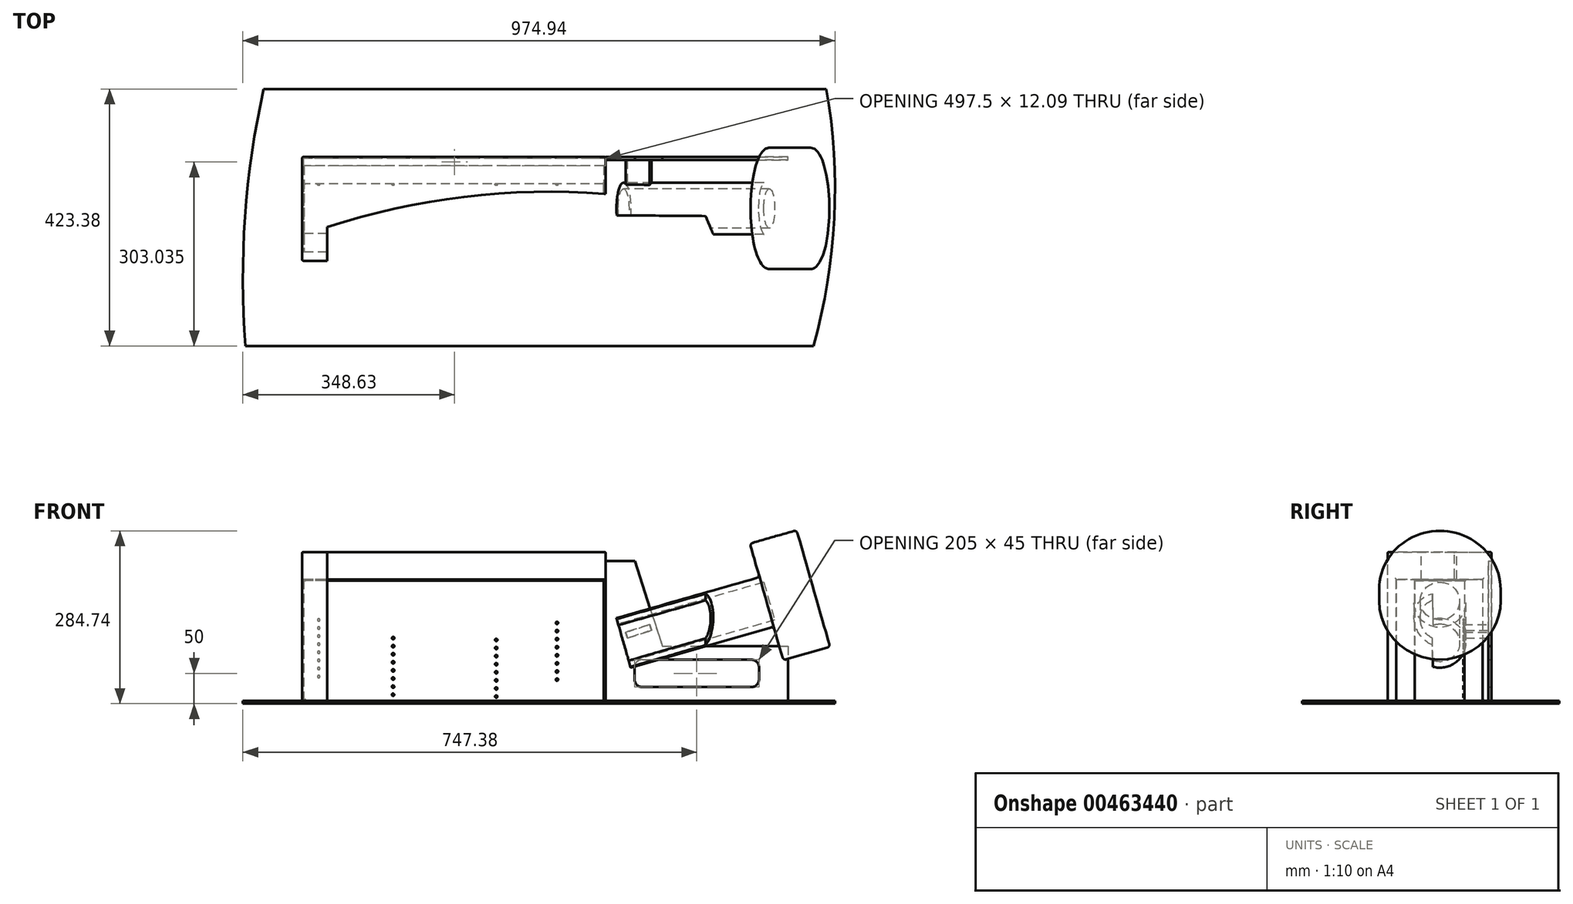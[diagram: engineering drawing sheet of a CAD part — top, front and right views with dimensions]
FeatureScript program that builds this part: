
annotation { "Feature Type Name" : "Feature", "Feature Type Description" : "" }
export const myFeature = defineFeature(function(context is Context, id is Id, definition is map)
    precondition{}
    {
        {
            var Q0;
            Q0=qCreatedBy(makeId("Right.planeOp"),FACE);
            var sketch = newSketch(context, id + "F0", { "sketchPlane" : qUnion([Q0])});
            skLineSegment(sketch, "E0.top", {"start": v(-171.18, 245.1) * mm, "end": v(0, 245.1) * mm});
            skLineSegment(sketch, "E0.left", {"start": v(-171.18, 0) * mm, "end": v(-171.18, 245.1) * mm});
            skLineSegment(sketch, "E0.right", {"start": v(0, 0) * mm, "end": v(0, 245.1) * mm});
            skLineSegment(sketch, "E1", {"start": v(-171.18, 0) * mm, "end": v(-156.6, 0) * mm});
            skLineSegment(sketch, "E2", {"start": v(-156.6, 0) * mm, "end": v(-156.6, 200) * mm});
            skLineSegment(sketch, "E3", {"start": v(-156.6, 200) * mm, "end": v(-14.59, 200) * mm});
            skLineSegment(sketch, "E4", {"start": v(-14.59, 200) * mm, "end": v(-14.59, 0) * mm});
            skLineSegment(sketch, "E5", {"start": v(-14.59, 0) * mm, "end": v(0, 0) * mm});
            skSolve(sketch);
        }
        {
            var Q0;
            Q0=makeQuery(id+"F0.imprint","IMPRINT",FACE,{"disambiguationData":[TD([[makeQuery(id+"F0.imprint","IMPRINT",EDGE,{"derivedFrom":sQuery(id+"F0.wireOp",EDGE,"E0.top")}),-1.0]])]});
            extrude(context, id + "F1", {"entities" : qUnion([Q0]), "depth" : 496.5 * mm, "hasSecondDirection" : true, "secondDirectionOppositeDirection" : true, "secondDirectionDepth" : 3.5 * mm});
        }
        {
            var Q0;
            Q0=qCreatedBy(makeId("Right.planeOp"),FACE);
            var sketch = newSketch(context, id + "F2", { "sketchPlane" : qUnion([Q0])});
            skLineSegment(sketch, "E6.bottom", {"start": v(-14.59, 0) * mm, "end": v(-44.59, 0) * mm});
            skLineSegment(sketch, "E6.top", {"start": v(-14.6, 200) * mm, "end": v(-156.6, 200) * mm});
            skLineSegment(sketch, "E6.left", {"start": v(-14.59, 0) * mm, "end": v(-14.6, 200) * mm});
            skLineSegment(sketch, "E6.right", {"start": v(-156.59, 0) * mm, "end": v(-156.6, 200) * mm});
            skLineSegment(sketch, "E7", {"start": v(-126.59, 0) * mm, "end": v(-126.59, 198) * mm});
            skLineSegment(sketch, "E8", {"start": v(-126.59, 198) * mm, "end": v(-44.6, 198) * mm});
            skLineSegment(sketch, "E9", {"start": v(-44.6, 198) * mm, "end": v(-44.59, 0) * mm});
            skLineSegment(sketch, "E10.trimOffspring", {"start": v(-126.59, 0) * mm, "end": v(-156.59, 0) * mm});
            skSolve(sketch);
        }
        {
            var Q0;
            Q0 = qSketchRegion(id + "F2", true);
            extrude(context, id + "F3", {"entities" : qUnion([Q0]), "depth" : 493 * mm});
        }
        {
            var Q0;
            Q0=makeQuery(id+"F1.opExtrude","SWEPT_FACE",FACE,{"disambiguationData":[OSD([sQuery(id+"F0.wireOp",EDGE,"E0.top")])]});
            var sketch = newSketch(context, id + "F4", { "sketchPlane" : qUnion([Q0])});
            skLineSegment(sketch, "E11", {"start": v(37.8, -115.66) * mm, "end": v(37.8, -234.3) * mm});
            skLineSegment(sketch, "E12", {"start": v(37.8, -234.3) * mm, "end": v(505.15, -234.3) * mm});
            skLineSegment(sketch, "E13", {"start": v(509.32, -61.9) * mm, "end": v(505.15, -234.3) * mm});
            skArc(sketch, "E14", {"start": v(509.32, -61.9) * mm, "mid": v(270.84, -64.96) * mm, "end": v(37.8, -115.66) * mm});
            skSolve(sketch);
        }
        {
            var Q0;
            {var subQ0=sQuery(id+"F4.wireOp",EDGE,"E14");var subQ1=sQuery(id+"F4.wireOp",EDGE,"E11");var subQ2=makeQuery(id+"F4.imprint","INTERSECT",VERTEX,{"derivedFrom":[subQ1,subQ0]});Q0=makeQuery(id+"F4.imprint","IMPRINT",FACE,{"disambiguationData":[TD([[makeQuery(id+"F4.imprint","IMPRINT",EDGE,{"disambiguationData":[TD([[subQ2,1.0]])],"derivedFrom":subQ0}),1.0]])]});}
            extrude(context, id + "F5", {"entities" : qUnion([Q0]), "operationType" : NewBodyOperationType.REMOVE, "endBound" : BoundingType.THROUGH_ALL, "oppositeDirection" : true, "depth" : 25 * mm, "hasSecondDirection" : true, "secondDirectionBound" : SecondDirectionBoundingType.THROUGH_ALL, "secondDirectionOppositeDirection" : false, "secondDirectionDepth" : 25 * mm});
        }
        {
            var Q0;
            Q0=makeQuery(id+"F3.opExtrude","SWEPT_FACE",FACE,{"disambiguationData":[OSD([sQuery(id+"F2.wireOp",EDGE,"E9")])]});
            var sketch = newSketch(context, id + "F6", { "sketchPlane" : qUnion([Q0])});
            skCircle(sketch, "E15", {"center": v(24, 39.75) * mm, "radius": 2 * mm});
            skCircle(sketch, "E16.1.0.0", {"center": v(24, 53.1) * mm, "radius": 2 * mm});
            skCircle(sketch, "E16.2.0.0", {"center": v(24, 66.43) * mm, "radius": 2 * mm});
            skCircle(sketch, "E16.3.0.0", {"center": v(24, 79.77) * mm, "radius": 2 * mm});
            skCircle(sketch, "E16.4.0.0", {"center": v(24, 93.11) * mm, "radius": 2 * mm});
            skCircle(sketch, "E16.5.0.0", {"center": v(24, 106.45) * mm, "radius": 2 * mm});
            skCircle(sketch, "E16.6.0.0", {"center": v(24, 119.79) * mm, "radius": 2 * mm});
            skCircle(sketch, "E16.7.0.0", {"center": v(24, 133.13) * mm, "radius": 2 * mm});
            skLineSegment(sketch, "E16.direction1", {"start": v(24, 39.75) * mm, "end": v(24, 53.1) * mm, "construction": true});
            skCircle(sketch, "E17", {"center": v(146.3, 9.75) * mm, "radius": 2 * mm});
            skCircle(sketch, "E18.1.0.0", {"center": v(146.35, 23.09) * mm, "radius": 2 * mm});
            skCircle(sketch, "E18.2.0.0", {"center": v(146.4, 36.43) * mm, "radius": 2 * mm});
            skCircle(sketch, "E18.3.0.0", {"center": v(146.46, 49.77) * mm, "radius": 2 * mm});
            skCircle(sketch, "E18.4.0.0", {"center": v(146.51, 63.1) * mm, "radius": 2 * mm});
            skCircle(sketch, "E18.5.0.0", {"center": v(146.57, 76.45) * mm, "radius": 2 * mm});
            skCircle(sketch, "E18.6.0.0", {"center": v(146.62, 89.79) * mm, "radius": 2 * mm});
            skCircle(sketch, "E18.7.0.0", {"center": v(146.67, 103.13) * mm, "radius": 2 * mm});
            skLineSegment(sketch, "E18.direction1", {"start": v(146.3, 9.75) * mm, "end": v(146.35, 23.09) * mm, "construction": true});
            skCircle(sketch, "E19", {"center": v(316.3, 6.75) * mm, "radius": 2 * mm});
            skCircle(sketch, "E20.0.1.0", {"center": v(316.3, 20.09) * mm, "radius": 2 * mm});
            skCircle(sketch, "E20.0.2.0", {"center": v(316.3, 33.43) * mm, "radius": 2 * mm});
            skCircle(sketch, "E20.0.3.0", {"center": v(316.3, 46.77) * mm, "radius": 2 * mm});
            skCircle(sketch, "E20.0.4.0", {"center": v(316.3, 60.1) * mm, "radius": 2 * mm});
            skCircle(sketch, "E20.0.5.0", {"center": v(316.3, 73.45) * mm, "radius": 2 * mm});
            skCircle(sketch, "E20.0.6.0", {"center": v(316.3, 86.79) * mm, "radius": 2 * mm});
            skCircle(sketch, "E20.0.7.0", {"center": v(316.3, 100.13) * mm, "radius": 2 * mm});
            skLineSegment(sketch, "E20.direction1", {"start": v(316.3, 6.75) * mm, "end": v(368.2, 6.75) * mm, "construction": true});
            skLineSegment(sketch, "E20.direction2", {"start": v(316.3, 6.75) * mm, "end": v(316.3, 20.09) * mm, "construction": true});
            skCircle(sketch, "E21", {"center": v(416.3, 34.75) * mm, "radius": 2 * mm});
            skCircle(sketch, "E22.0.1.0", {"center": v(416.3, 48.1) * mm, "radius": 2 * mm});
            skCircle(sketch, "E22.0.2.0", {"center": v(416.3, 61.43) * mm, "radius": 2 * mm});
            skCircle(sketch, "E22.0.3.0", {"center": v(416.3, 74.77) * mm, "radius": 2 * mm});
            skCircle(sketch, "E22.0.4.0", {"center": v(416.3, 88.11) * mm, "radius": 2 * mm});
            skCircle(sketch, "E22.0.5.0", {"center": v(416.3, 101.45) * mm, "radius": 2 * mm});
            skCircle(sketch, "E22.0.6.0", {"center": v(416.3, 114.79) * mm, "radius": 2 * mm});
            skCircle(sketch, "E22.0.7.0", {"center": v(416.3, 128.13) * mm, "radius": 2 * mm});
            skLineSegment(sketch, "E22.direction1", {"start": v(416.3, 34.75) * mm, "end": v(490.5, 34.75) * mm, "construction": true});
            skLineSegment(sketch, "E22.direction2", {"start": v(416.3, 34.75) * mm, "end": v(416.3, 48.1) * mm, "construction": true});
            skSolve(sketch);
        }
        {
            var Q0;
            Q0 = qSketchRegion(id + "F6", true);
            extrude(context, id + "F7", {"entities" : qUnion([Q0]), "depth" : 2 * mm});
        }
        {
            var Q0;
            Q0=makeQuery(id+"F1.opExtrude","SWEPT_EDGE",EDGE,{"disambiguationData":[OSD([sQuery(id+"F0.wireOp",EDGE,"E0.top"),sQuery(id+"F0.wireOp",EDGE,"E0.left")])]});
            var Q1;
            Q1=makeQuery(id+"F1.opExtrude","CAP_EDGE",EDGE,{"disambiguationData":[OSD([sQuery(id+"F0.wireOp",EDGE,"E0.top")])],"isStart":true});
            var Q2;
            Q2=makeQuery(id+"F1.opExtrude","SWEPT_EDGE",EDGE,{"disambiguationData":[OSD([sQuery(id+"F0.wireOp",EDGE,"E0.top"),sQuery(id+"F0.wireOp",EDGE,"E0.right")])]});
            var Q3;
            Q3=makeQuery(id+"F1.opExtrude","CAP_EDGE",EDGE,{"disambiguationData":[OSD([sQuery(id+"F0.wireOp",EDGE,"E0.left")])],"isStart":true});
            var Q4;
            Q4=makeQuery(id+"F1.opExtrude","CAP_EDGE",EDGE,{"disambiguationData":[OSD([sQuery(id+"F0.wireOp",EDGE,"E0.right")])],"isStart":false});
            var Q5;
            Q5=makeQuery(id+"F1.opExtrude","CAP_EDGE",EDGE,{"disambiguationData":[OSD([sQuery(id+"F0.wireOp",EDGE,"E0.top")])],"isStart":false});
            var Q6;
            Q6=makeQuery(id+"F1.opExtrude","CAP_EDGE",EDGE,{"disambiguationData":[OSD([sQuery(id+"F0.wireOp",EDGE,"E4")])],"isStart":false});
            var Q7;
            Q7=makeQuery(id+"F1.opExtrude","CAP_EDGE",EDGE,{"disambiguationData":[OSD([sQuery(id+"F0.wireOp",EDGE,"E3")])],"isStart":false});
            var Q8;
            Q8=makeQuery(id+"F1.opExtrude","SWEPT_EDGE",EDGE,{"disambiguationData":[OSD([sQuery(id+"F0.wireOp",EDGE,"E0.right"),sQuery(id+"F0.wireOp",EDGE,"E5")])]});
            var Q9;
            Q9=makeQuery(id+"F1.opExtrude","CAP_EDGE",EDGE,{"disambiguationData":[OSD([sQuery(id+"F0.wireOp",EDGE,"E0.right")])],"isStart":true});
            var Q10;
            Q10=makeQuery(id+"F1.opExtrude","CAP_EDGE",EDGE,{"disambiguationData":[OSD([sQuery(id+"F0.wireOp",EDGE,"E4")])],"isStart":true});
            var Q11;
            Q11=makeQuery(id+"F1.opExtrude","CAP_EDGE",EDGE,{"disambiguationData":[OSD([sQuery(id+"F0.wireOp",EDGE,"E3")])],"isStart":true});
            var Q12;
            Q12=makeQuery(id+"F1.opExtrude","CAP_EDGE",EDGE,{"disambiguationData":[OSD([sQuery(id+"F0.wireOp",EDGE,"E2")])],"isStart":true});
            var Q13;
            Q13=makeQuery(id+"F1.opExtrude","CAP_EDGE",EDGE,{"disambiguationData":[OSD([sQuery(id+"F0.wireOp",EDGE,"E1")])],"isStart":true});
            var Q14;
            Q14=makeQuery(id+"F1.opExtrude","SWEPT_EDGE",EDGE,{"disambiguationData":[OSD([sQuery(id+"F0.wireOp",EDGE,"E0.left"),sQuery(id+"F0.wireOp",EDGE,"E1")])]});
            var Q15;
            Q15=makeQuery(id+"F1.opExtrude","CAP_EDGE",EDGE,{"disambiguationData":[OSD([sQuery(id+"F0.wireOp",EDGE,"E5")])],"isStart":true});
            var Q16;
            Q16=makeQuery(id+"F3.opExtrude","CAP_EDGE",EDGE,{"disambiguationData":[OSD([sQuery(id+"F2.wireOp",EDGE,"E9")])],"isStart":true});
            var Q17;
            Q17=makeQuery(id+"F3.opExtrude","SWEPT_EDGE",EDGE,{"disambiguationData":[OSD([sQuery(id+"F2.wireOp",EDGE,"E6.bottom"),sQuery(id+"F2.wireOp",EDGE,"E9")])]});
            fillet(context, id + "F8", {"entities" : qUnion([Q0, Q1, Q2, Q3, Q4, Q5, Q6, Q7, Q8, Q9, Q10, Q11, Q12, Q13, Q14, Q15, Q16, Q17]), "radius" : 2.5 * mm, "tangentPropagation" : true, "allowEdgeOverflow" : false});
        }
        {
            var Q0;
            Q0=qCreatedBy(makeId("Front.planeOp"),FACE);
            var sketch = newSketch(context, id + "F9", { "sketchPlane" : qUnion([Q0])});
            skLineSegment(sketch, "E23", {"start": v(496.5, 0) * mm, "end": v(496.5, 230) * mm});
            skLineSegment(sketch, "E24", {"start": v(496.5, 230) * mm, "end": v(544.38, 230) * mm});
            skLineSegment(sketch, "E25", {"start": v(544.38, 230) * mm, "end": v(589.8, 90) * mm});
            skLineSegment(sketch, "E26", {"start": v(589.8, 90) * mm, "end": v(796.5, 90) * mm});
            skLineSegment(sketch, "E27", {"start": v(796.5, 90) * mm, "end": v(796.5, 0) * mm});
            skLineSegment(sketch, "E28", {"start": v(796.5, 0) * mm, "end": v(496.5, 0) * mm});
            skLineSegment(sketch, "E29.bottom", {"start": v(556.5, 67.5) * mm, "end": v(736.5, 67.5) * mm});
            skLineSegment(sketch, "E29.top", {"start": v(556.5, 22.5) * mm, "end": v(736.5, 22.5) * mm});
            skLineSegment(sketch, "E29.left", {"start": v(544, 55) * mm, "end": v(544, 35) * mm});
            skLineSegment(sketch, "E29.right", {"start": v(749, 55) * mm, "end": v(749, 35) * mm});
            skPoint(sketch, "E30.visualSharp", {"position": v(544, 67.5) * mm});
            skArc(sketch, "E30.filletArc", {"start": v(556.5, 67.5) * mm, "mid": v(547.66, 63.84) * mm, "end": v(544, 55) * mm});
            skPoint(sketch, "E31.visualSharp", {"position": v(749, 67.5) * mm});
            skArc(sketch, "E31.filletArc", {"start": v(749, 55) * mm, "mid": v(745.34, 63.84) * mm, "end": v(736.5, 67.5) * mm});
            skPoint(sketch, "E32.visualSharp", {"position": v(749, 22.5) * mm});
            skArc(sketch, "E32.filletArc", {"start": v(736.5, 22.5) * mm, "mid": v(745.34, 26.16) * mm, "end": v(749, 35) * mm});
            skPoint(sketch, "E33.visualSharp", {"position": v(544, 22.5) * mm});
            skArc(sketch, "E33.filletArc", {"start": v(544, 35) * mm, "mid": v(547.66, 26.16) * mm, "end": v(556.5, 22.5) * mm});
            skSolve(sketch);
        }
        {
            var Q0;
            Q0 = qSketchRegion(id + "F9", true);
            extrude(context, id + "F10", {"entities" : qUnion([Q0]), "depth" : 5 * mm});
        }
        {
            var Q0;
            Q0=makeQuery(id+"F10.opExtrude","CAP_FACE",FACE,{"disambiguationData":[OSD([sQuery(id+"F9.wireOp",EDGE,"E23"),sQuery(id+"F9.wireOp",EDGE,"E24"),sQuery(id+"F9.wireOp",EDGE,"E25"),sQuery(id+"F9.wireOp",EDGE,"E26"),sQuery(id+"F9.wireOp",EDGE,"E27"),sQuery(id+"F9.wireOp",EDGE,"E28"),sQuery(id+"F9.wireOp",EDGE,"E29.bottom"),sQuery(id+"F9.wireOp",EDGE,"E29.top"),sQuery(id+"F9.wireOp",EDGE,"E29.left"),sQuery(id+"F9.wireOp",EDGE,"E29.right"),sQuery(id+"F9.wireOp",EDGE,"E30.filletArc"),sQuery(id+"F9.wireOp",EDGE,"E31.filletArc"),sQuery(id+"F9.wireOp",EDGE,"E32.filletArc"),sQuery(id+"F9.wireOp",EDGE,"E33.filletArc")])],"isStart":false});
            cPlane(context, id + "F11", {"entities" : qUnion([Q0]), "cplaneType" : CPlaneType.OFFSET, "offset" : 80 * mm, "width" : 150 * mm, "height" : 150 * mm});
        }
        {
            var Q0;
            Q0=qCreatedBy(id+"F11.planeOp",FACE);
            var sketch = newSketch(context, id + "F12", { "sketchPlane" : qUnion([Q0])});
            skLineSegment(sketch, "E34", {"start": v(121.27, 85.77) * mm, "end": v(1213.1, 85.77) * mm, "construction": true});
            skLineSegment(sketch, "E35", {"start": v(226.38, 9.32) * mm, "end": v(1190.67, 285.82) * mm, "construction": true});
            skLineSegment(sketch, "E36", {"start": v(838.36, 184.8) * mm, "end": v(812.17, 276.12) * mm});
            skLineSegment(sketch, "E37", {"start": v(805.99, 279.55) * mm, "end": v(738.7, 260.25) * mm});
            skLineSegment(sketch, "E38", {"start": v(735.27, 254.07) * mm, "end": v(748.36, 208.4) * mm});
            skLineSegment(sketch, "E39", {"start": v(744.93, 202.22) * mm, "end": v(514.23, 136.07) * mm});
            skLineSegment(sketch, "E40", {"start": v(514.23, 136.07) * mm, "end": v(516.99, 126.46) * mm});
            skLineSegment(sketch, "E41", {"start": v(516.99, 126.46) * mm, "end": v(756.84, 195.23) * mm});
            skLineSegment(sketch, "E42", {"start": v(756.84, 195.23) * mm, "end": v(765.8, 164) * mm});
            skPoint(sketch, "E43.visualSharp", {"position": v(733.9, 258.87) * mm});
            skArc(sketch, "E43.filletArc", {"start": v(738.7, 260.25) * mm, "mid": v(735.7, 257.87) * mm, "end": v(735.27, 254.07) * mm});
            skPoint(sketch, "E44.visualSharp", {"position": v(810.8, 280.93) * mm});
            skArc(sketch, "E44.filletArc", {"start": v(812.17, 276.12) * mm, "mid": v(809.79, 279.11) * mm, "end": v(805.99, 279.55) * mm});
            skLineSegment(sketch, "E45", {"start": v(765.8, 164) * mm, "end": v(838.36, 184.8) * mm});
            skPoint(sketch, "E46.visualSharp", {"position": v(749.74, 203.6) * mm});
            skArc(sketch, "E46.filletArc", {"start": v(744.93, 202.22) * mm, "mid": v(747.93, 204.6) * mm, "end": v(748.36, 208.4) * mm});
            skSolve(sketch);
        }
        {
            var Q0;
            Q0 = qSketchRegion(id + "F12", true);
            var Q1;
            Q1=sQuery(id+"F12.wireOp",EDGE,"E35");
            revolve(context, id + "F13", {"entities" : qUnion([Q0]), "axis" : qUnion([Q1]), "revolveType" : RevolveType.FULL});
        }
        {
            var Q0;
            Q0=makeQuery(id+"F10.opExtrude","CAP_FACE",FACE,{"disambiguationData":[OSD([sQuery(id+"F9.wireOp",EDGE,"E23"),sQuery(id+"F9.wireOp",EDGE,"E24"),sQuery(id+"F9.wireOp",EDGE,"E25"),sQuery(id+"F9.wireOp",EDGE,"E26"),sQuery(id+"F9.wireOp",EDGE,"E27"),sQuery(id+"F9.wireOp",EDGE,"E28"),sQuery(id+"F9.wireOp",EDGE,"E29.bottom"),sQuery(id+"F9.wireOp",EDGE,"E29.top"),sQuery(id+"F9.wireOp",EDGE,"E29.left"),sQuery(id+"F9.wireOp",EDGE,"E29.right"),sQuery(id+"F9.wireOp",EDGE,"E30.filletArc"),sQuery(id+"F9.wireOp",EDGE,"E31.filletArc"),sQuery(id+"F9.wireOp",EDGE,"E32.filletArc"),sQuery(id+"F9.wireOp",EDGE,"E33.filletArc")])],"isStart":false});
            var sketch = newSketch(context, id + "F14", { "sketchPlane" : qUnion([Q0])});
            skLineSegment(sketch, "E47", {"start": v(529.2, 112.68) * mm, "end": v(532.32, 103.06) * mm});
            skLineSegment(sketch, "E48", {"start": v(532.32, 103.06) * mm, "end": v(572.12, 115.97) * mm});
            skLineSegment(sketch, "E49", {"start": v(572.12, 115.97) * mm, "end": v(569, 125.6) * mm});
            skLineSegment(sketch, "E50", {"start": v(569, 125.6) * mm, "end": v(529.2, 112.68) * mm});
            skSolve(sketch);
        }
        {
            var Q0;
            Q0 = qSketchRegion(id + "F14", true);
            extrude(context, id + "F15", {"entities" : qUnion([Q0]), "operationType" : NewBodyOperationType.ADD, "endBound" : BoundingType.UP_TO_NEXT, "depth" : 25 * mm});
        }
        {
            var Q0;
            Q0=makeQuery(id+"F1.opExtrude","SWEPT_FACE",FACE,{"disambiguationData":[OSD([sQuery(id+"F0.wireOp",EDGE,"E0.top")])]});
            var sketch = newSketch(context, id + "F16", { "sketchPlane" : qUnion([Q0])});
            skLineSegment(sketch, "E51", {"start": v(497.63, -96.17) * mm, "end": v(497.1, -162.12) * mm});
            skLineSegment(sketch, "E52", {"start": v(497.1, -162.12) * mm, "end": v(688.05, -162.12) * mm});
            skLineSegment(sketch, "E53", {"start": v(497.63, -96.17) * mm, "end": v(660.9, -97.49) * mm});
            skLineSegment(sketch, "E54", {"start": v(660.9, -97.49) * mm, "end": v(688.05, -162.12) * mm});
            skSolve(sketch);
        }
        {
            var Q0;
            Q0 = qSketchRegion(id + "F16", true);
            extrude(context, id + "F17", {"entities" : qUnion([Q0]), "operationType" : NewBodyOperationType.REMOVE, "endBound" : BoundingType.THROUGH_ALL, "oppositeDirection" : true, "depth" : 25 * mm});
        }
        {
            var Q0;
            Q0=makeQuery(id+"F1.opExtrude","SWEPT_FACE",FACE,{"disambiguationData":[OSD([sQuery(id+"F0.wireOp",EDGE,"E5")])]});
            var sketch = newSketch(context, id + "F18", { "sketchPlane" : qUnion([Q0])});
            skLineSegment(sketch, "E55.bottom", {"start": v(-96.48, 311.58) * mm, "end": v(838.57, 311.58) * mm});
            skLineSegment(sketch, "E55.top", {"start": v(-66.7, -111.8) * mm, "end": v(859.85, -111.8) * mm});
            skArc(sketch, "E56", {"start": v(-96.48, 311.58) * mm, "mid": v(-97.35, 98.78) * mm, "end": v(-66.7, -111.8) * mm});
            skArc(sketch, "E57", {"start": v(859.85, -111.8) * mm, "mid": v(872.85, 101.08) * mm, "end": v(838.57, 311.58) * mm});
            skSolve(sketch);
        }
        {
            var Q0;
            Q0=makeQuery(id+"F18.imprint","IMPRINT",FACE,{"disambiguationData":[TD([[makeQuery(id+"F18.imprint","IMPRINT",EDGE,{"derivedFrom":sQuery(id+"F18.wireOp",EDGE,"E55.bottom")}),-1.0]])]});
            extrude(context, id + "F19", {"entities" : qUnion([Q0]), "depth" : 5 * mm});
        }
    });
